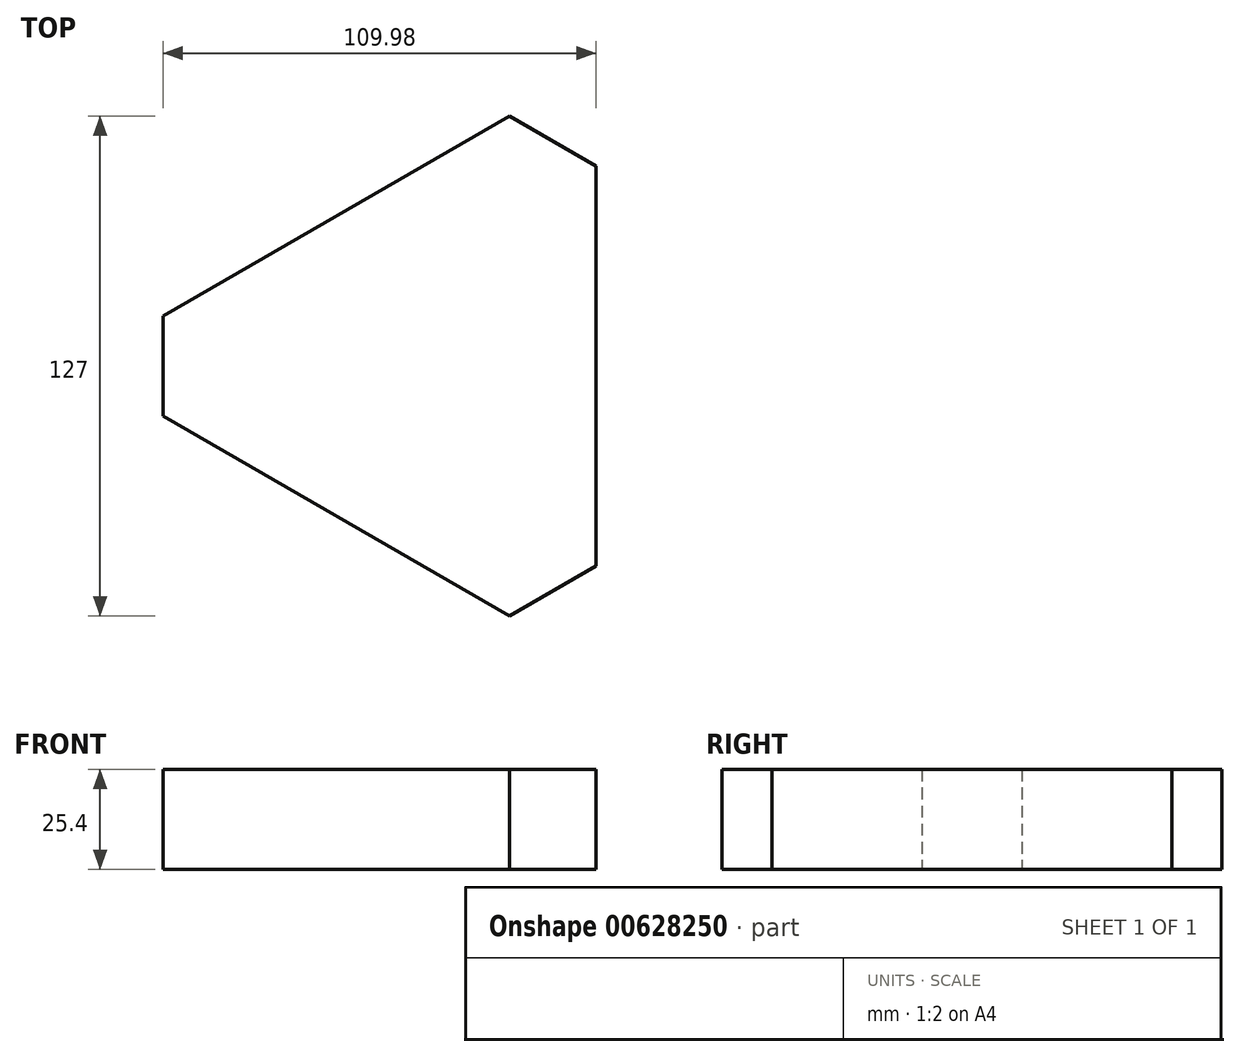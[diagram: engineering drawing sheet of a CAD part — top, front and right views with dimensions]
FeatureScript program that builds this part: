
annotation { "Feature Type Name" : "Feature", "Feature Type Description" : "" }
export const myFeature = defineFeature(function(context is Context, id is Id, definition is map)
    precondition{}
    {
        {
            var Q0;
            Q0=qCreatedBy(makeId("Top.planeOp"),FACE);
            var sketch = newSketch(context, id + "F0", { "sketchPlane" : qUnion([Q0])});
            skCircle(sketch, "E0.cCircle", {"center": v(0, 0) * mm, "radius": 44 * mm, "construction": true});
            skLineSegment(sketch, "E0.0", {"start": v(44, 25.4) * mm, "end": v(44, -25.4) * mm});
            skLineSegment(sketch, "E0.2", {"start": v(0, -50.8) * mm, "end": v(-44, -25.4) * mm});
            skLineSegment(sketch, "E0.4", {"start": v(-44, 25.4) * mm, "end": v(0, 50.8) * mm});
            skPoint(sketch, "E0.0.midPoint", {"position": v(44, 0) * mm});
            skLineSegment(sketch, "E1", {"start": v(0, 50.8) * mm, "end": v(22, 63.5) * mm});
            skLineSegment(sketch, "E2", {"start": v(44, 25.4) * mm, "end": v(44, 50.8) * mm});
            skLineSegment(sketch, "E3", {"start": v(22, 63.5) * mm, "end": v(44, 50.8) * mm});
            skLineSegment(sketch, "E4", {"start": v(44, -25.4) * mm, "end": v(44, -50.8) * mm});
            skLineSegment(sketch, "E5", {"start": v(0, -50.8) * mm, "end": v(22, -63.5) * mm});
            skLineSegment(sketch, "E6", {"start": v(22, -63.5) * mm, "end": v(44, -50.8) * mm});
            skLineSegment(sketch, "E7", {"start": v(-44, 25.4) * mm, "end": v(-66, 12.7) * mm});
            skLineSegment(sketch, "E8", {"start": v(-44, -25.4) * mm, "end": v(-66, -12.7) * mm});
            skLineSegment(sketch, "E9", {"start": v(-66, -12.7) * mm, "end": v(-66, 12.7) * mm});
            skSolve(sketch);
        }
        {
            var Q0;
            Q0=makeQuery(id+"F0.imprint","IMPRINT",FACE,{"disambiguationData":[TD([[makeQuery(id+"F0.imprint","IMPRINT",EDGE,{"derivedFrom":sQuery(id+"F0.wireOp",EDGE,"E0.0")}),-1.0]])]});
            extrude(context, id + "F1", {"entities" : qUnion([Q0]), "depth" : 25.4 * mm, "offsetDistance" : 25.4 * mm});
        }
    });
